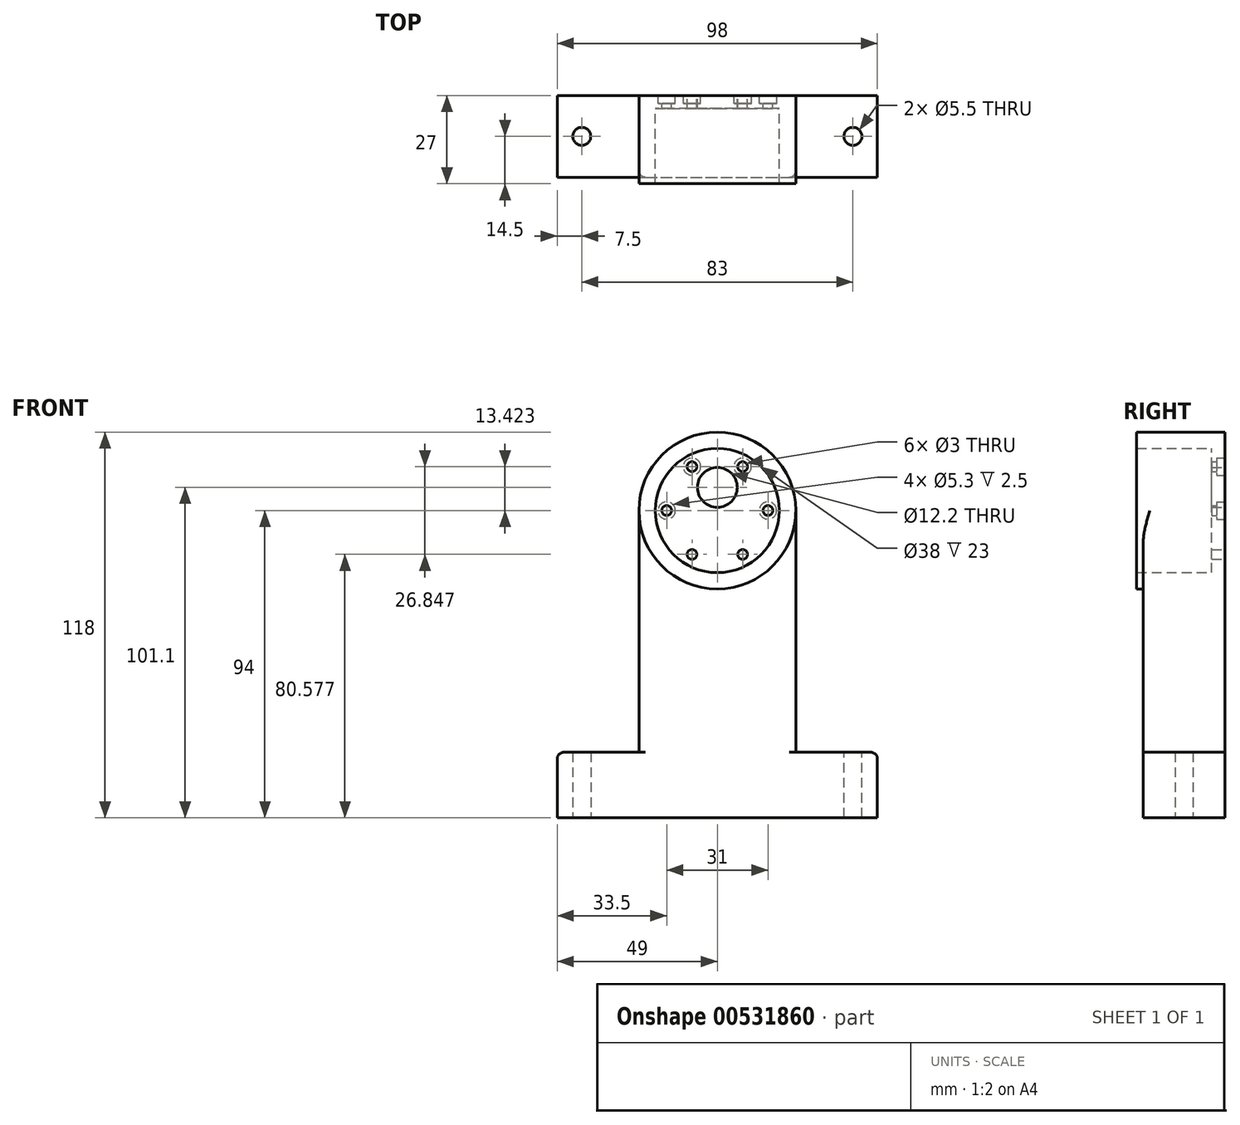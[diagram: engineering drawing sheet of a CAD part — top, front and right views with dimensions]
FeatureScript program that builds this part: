
annotation { "Feature Type Name" : "Feature", "Feature Type Description" : "" }
export const myFeature = defineFeature(function(context is Context, id is Id, definition is map)
    precondition{}
    {
        {
            var Q0;
            Q0=qCreatedBy(makeId("Front.planeOp"),FACE);
            var sketch = newSketch(context, id + "F0", { "sketchPlane" : qUnion([Q0])});
            skCircle(sketch, "E0", {"center": v(0, 0) * mm, "radius": 19 * mm});
            skCircle(sketch, "E1", {"center": v(0, 7.1) * mm, "radius": 6.1 * mm});
            skLineSegment(sketch, "E2", {"start": v(0, 0) * mm, "end": v(15.5, 0) * mm});
            skCircle(sketch, "E3", {"center": v(15.5, 0) * mm, "radius": 1.5 * mm});
            skCircle(sketch, "E4.1.0", {"center": v(7.75, 13.42) * mm, "radius": 1.5 * mm});
            skCircle(sketch, "E4.2.0", {"center": v(-7.75, 13.42) * mm, "radius": 1.5 * mm});
            skCircle(sketch, "E4.3.0", {"center": v(-15.5, 0) * mm, "radius": 1.5 * mm});
            skCircle(sketch, "E4.4.0", {"center": v(-7.75, -13.42) * mm, "radius": 1.5 * mm});
            skCircle(sketch, "E4.5.0", {"center": v(7.75, -13.42) * mm, "radius": 1.5 * mm});
            skSolve(sketch);
        }
        {
            var Q0;
            Q0=qSketchRegion(id+"F0",true);
            extrude(context, id + "F1", {"entities" : qUnion([Q0]), "depth" : 4 * mm});
        }
        {
            var Q0;
            Q0=qCreatedBy(makeId("Front.planeOp"),FACE);
            var sketch = newSketch(context, id + "F2", { "sketchPlane" : qUnion([Q0])});
            skCircle(sketch, "E5", {"center": v(0, 0) * mm, "radius": 19 * mm});
            skCircle(sketch, "E6", {"center": v(0, 0) * mm, "radius": 24 * mm});
            skSolve(sketch);
        }
        {
            var Q0;
            Q0=qSketchRegion(id+"F2",true);
            extrude(context, id + "F3", {"entities" : qUnion([Q0]), "operationType" : NewBodyOperationType.ADD, "depth" : 27 * mm});
        }
        {
            var Q0;
            Q0=makeQuery(id+"F3.boolean.opBoolean","MERGE",FACE,{"derivedFrom":[makeQuery(id+"F1.opExtrude","CAP_FACE",FACE,{"disambiguationData":[OSD([sQuery(id+"F0.wireOp",EDGE,"E0"),sQuery(id+"F0.wireOp",EDGE,"E1"),sQuery(id+"F0.wireOp",EDGE,"E3"),sQuery(id+"F0.wireOp",EDGE,"E4.1.0"),sQuery(id+"F0.wireOp",EDGE,"E4.2.0"),sQuery(id+"F0.wireOp",EDGE,"E4.3.0"),sQuery(id+"F0.wireOp",EDGE,"E4.4.0"),sQuery(id+"F0.wireOp",EDGE,"E4.5.0")])],"isStart":true}),makeQuery(id+"F3.opExtrude","CAP_FACE",FACE,{"disambiguationData":[OSD([sQuery(id+"F2.wireOp",EDGE,"E5"),sQuery(id+"F2.wireOp",EDGE,"E6")])],"isStart":true})]});
            var sketch = newSketch(context, id + "F4", { "sketchPlane" : qUnion([Q0])});
            skLineSegment(sketch, "E7", {"start": v(24, 0) * mm, "end": v(24, -40) * mm});
            skLineSegment(sketch, "E8", {"start": v(24, -40) * mm, "end": v(0, -40) * mm});
            skLineSegment(sketch, "E9", {"start": v(-24, 0) * mm, "end": v(-24, -40) * mm});
            skLineSegment(sketch, "E10", {"start": v(-24, -40) * mm, "end": v(0, -40) * mm});
            skArc(sketch, "E11", {"start": v(-24, 0) * mm, "mid": v(0, -24) * mm, "end": v(24, 0) * mm});
            skSolve(sketch);
        }
        {
            var Q0;
            Q0=qSketchRegion(id+"F4",true);
            extrude(context, id + "F5", {"entities" : qUnion([Q0]), "operationType" : NewBodyOperationType.ADD, "oppositeDirection" : true, "depth" : 25 * mm});
        }
        {
            var Q0;
            Q0=makeQuery(id+"F5.boolean.opBoolean","MERGE",FACE,{"derivedFrom":[makeQuery(id+"F3.boolean.opBoolean","MERGE",FACE,{"derivedFrom":[makeQuery(id+"F1.opExtrude","CAP_FACE",FACE,{"disambiguationData":[OSD([sQuery(id+"F0.wireOp",EDGE,"E0"),sQuery(id+"F0.wireOp",EDGE,"E1"),sQuery(id+"F0.wireOp",EDGE,"E3"),sQuery(id+"F0.wireOp",EDGE,"E4.1.0"),sQuery(id+"F0.wireOp",EDGE,"E4.2.0"),sQuery(id+"F0.wireOp",EDGE,"E4.3.0"),sQuery(id+"F0.wireOp",EDGE,"E4.4.0"),sQuery(id+"F0.wireOp",EDGE,"E4.5.0")])],"isStart":true}),makeQuery(id+"F3.opExtrude","CAP_FACE",FACE,{"disambiguationData":[OSD([sQuery(id+"F2.wireOp",EDGE,"E5"),sQuery(id+"F2.wireOp",EDGE,"E6")])],"isStart":true})]}),makeQuery(id+"F5.opExtrude","CAP_FACE",FACE,{"disambiguationData":[OSD([sQuery(id+"F4.wireOp",EDGE,"E7"),sQuery(id+"F4.wireOp",EDGE,"E8"),sQuery(id+"F4.wireOp",EDGE,"E9"),sQuery(id+"F4.wireOp",EDGE,"E10"),sQuery(id+"F4.wireOp",EDGE,"E11")])],"isStart":true})]});
            var sketch = newSketch(context, id + "F6", { "sketchPlane" : qUnion([Q0])});
            skCircle(sketch, "E12", {"center": v(-7.75, 13.42) * mm, "radius": 2.65 * mm});
            skCircle(sketch, "E13", {"center": v(7.75, 13.42) * mm, "radius": 2.65 * mm});
            skCircle(sketch, "E14", {"center": v(-15.5, 0) * mm, "radius": 2.65 * mm});
            skCircle(sketch, "E15", {"center": v(15.5, 0) * mm, "radius": 2.65 * mm});
            skSolve(sketch);
        }
        {
            var Q0;
            Q0=qSketchRegion(id+"F6",true);
            extrude(context, id + "F7", {"entities" : qUnion([Q0]), "operationType" : NewBodyOperationType.REMOVE, "oppositeDirection" : true, "depth" : 2.5 * mm});
        }
        {
            var Q0;
            Q0=makeQuery(id+"F5.opExtrude","CAP_FACE",FACE,{"disambiguationData":[OSD([sQuery(id+"F4.wireOp",EDGE,"E7"),sQuery(id+"F4.wireOp",EDGE,"E8"),sQuery(id+"F4.wireOp",EDGE,"E9"),sQuery(id+"F4.wireOp",EDGE,"E10"),sQuery(id+"F4.wireOp",EDGE,"E11")])],"isStart":false});
            var sketch = newSketch(context, id + "F8", { "sketchPlane" : qUnion([Q0])});
            skLineSegment(sketch, "E16", {"start": v(0, 0) * mm, "end": v(0, -19) * mm});
            skLineSegment(sketch, "E17", {"start": v(0, -19) * mm, "end": v(0, -94) * mm});
            skPoint(sketch, "E17.endSnap0", {"position": v(0, -40) * mm});
            skLineSegment(sketch, "E18.bottom", {"start": v(0, -94) * mm, "end": v(24, -94) * mm});
            skLineSegment(sketch, "E18.top", {"start": v(0, -40) * mm, "end": v(24, -40) * mm});
            skLineSegment(sketch, "E18.left", {"start": v(0, -94) * mm, "end": v(0, -40) * mm});
            skLineSegment(sketch, "E18.right", {"start": v(24, -94) * mm, "end": v(24, -40) * mm});
            skLineSegment(sketch, "E19.bottom", {"start": v(0, -94) * mm, "end": v(-24, -94) * mm});
            skLineSegment(sketch, "E19.top", {"start": v(0, -40) * mm, "end": v(-24, -40) * mm});
            skLineSegment(sketch, "E19.right", {"start": v(-24, -94) * mm, "end": v(-24, -40) * mm});
            skSolve(sketch);
        }
        {
            var Q0;
            Q0=qSketchRegion(id+"F8",true);
            var Q1;
            Q1=makeQuery(id+"F5.boolean.opBoolean","MERGE",FACE,{"derivedFrom":[makeQuery(id+"F3.boolean.opBoolean","MERGE",FACE,{"derivedFrom":[makeQuery(id+"F1.opExtrude","CAP_FACE",FACE,{"disambiguationData":[OSD([sQuery(id+"F0.wireOp",EDGE,"E0"),sQuery(id+"F0.wireOp",EDGE,"E1"),sQuery(id+"F0.wireOp",EDGE,"E3"),sQuery(id+"F0.wireOp",EDGE,"E4.1.0"),sQuery(id+"F0.wireOp",EDGE,"E4.2.0"),sQuery(id+"F0.wireOp",EDGE,"E4.3.0"),sQuery(id+"F0.wireOp",EDGE,"E4.4.0"),sQuery(id+"F0.wireOp",EDGE,"E4.5.0")])],"isStart":true}),makeQuery(id+"F3.opExtrude","CAP_FACE",FACE,{"disambiguationData":[OSD([sQuery(id+"F2.wireOp",EDGE,"E5"),sQuery(id+"F2.wireOp",EDGE,"E6")])],"isStart":true})]}),makeQuery(id+"F5.opExtrude","CAP_FACE",FACE,{"disambiguationData":[OSD([sQuery(id+"F4.wireOp",EDGE,"E7"),sQuery(id+"F4.wireOp",EDGE,"E8"),sQuery(id+"F4.wireOp",EDGE,"E9"),sQuery(id+"F4.wireOp",EDGE,"E10"),sQuery(id+"F4.wireOp",EDGE,"E11")])],"isStart":true})]});
            extrude(context, id + "F9", {"entities" : qUnion([Q0]), "operationType" : NewBodyOperationType.ADD, "endBound" : BoundingType.UP_TO_SURFACE, "oppositeDirection" : true, "endBoundEntityFace" : qUnion([Q1]), "depth" : 25 * mm});
        }
        {
            var Q0;
            Q0=makeQuery(id+"F9.boolean.opBoolean","MERGE",FACE,{"derivedFrom":[makeQuery(id+"F5.opExtrude","SWEPT_FACE",FACE,{"disambiguationData":[OSD([sQuery(id+"F4.wireOp",EDGE,"E9")])]}),makeQuery(id+"F9.opExtrude","SWEPT_FACE",FACE,{"disambiguationData":[OSD([sQuery(id+"F8.wireOp",EDGE,"E18.right")])]})]});
            var sketch = newSketch(context, id + "F10", { "sketchPlane" : qUnion([Q0])});
            skLineSegment(sketch, "E20.bottom", {"start": v(-25, -94) * mm, "end": v(0, -94) * mm});
            skLineSegment(sketch, "E20.top", {"start": v(-25, -74) * mm, "end": v(0, -74) * mm});
            skLineSegment(sketch, "E20.left", {"start": v(-25, -94) * mm, "end": v(-25, -74) * mm});
            skLineSegment(sketch, "E20.right", {"start": v(0, -94) * mm, "end": v(0, -74) * mm});
            skSolve(sketch);
        }
        {
            var Q0;
            Q0=qSketchRegion(id+"F10",true);
            extrude(context, id + "F11", {"entities" : qUnion([Q0]), "operationType" : NewBodyOperationType.ADD, "depth" : 25 * mm});
        }
        {
            var Q0;
            Q0=makeQuery(id+"F11.opExtrude","SWEPT_FACE",FACE,{"disambiguationData":[OSD([sQuery(id+"F10.wireOp",EDGE,"E20.top")])]});
            var sketch = newSketch(context, id + "F12", { "sketchPlane" : qUnion([Q0])});
            skLineSegment(sketch, "E21", {"start": v(49, -12.5) * mm, "end": v(34, -12.5) * mm});
            skCircle(sketch, "E22", {"center": v(41.5, -12.5) * mm, "radius": 2.75 * mm});
            skSolve(sketch);
        }
        {
            var Q0;
            Q0=makeQuery(id+"F9.boolean.opBoolean","MERGE",FACE,{"derivedFrom":[makeQuery(id+"F5.opExtrude","SWEPT_FACE",FACE,{"disambiguationData":[OSD([sQuery(id+"F4.wireOp",EDGE,"E7")])]}),makeQuery(id+"F9.opExtrude","SWEPT_FACE",FACE,{"disambiguationData":[OSD([sQuery(id+"F8.wireOp",EDGE,"E19.right")])]})]});
            var sketch = newSketch(context, id + "F13", { "sketchPlane" : qUnion([Q0])});
            skLineSegment(sketch, "E23.bottom", {"start": v(25, -94) * mm, "end": v(0, -94) * mm});
            skLineSegment(sketch, "E23.top", {"start": v(25, -74) * mm, "end": v(0, -74) * mm});
            skLineSegment(sketch, "E23.left", {"start": v(25, -94) * mm, "end": v(25, -74) * mm});
            skLineSegment(sketch, "E23.right", {"start": v(0, -94) * mm, "end": v(0, -74) * mm});
            skSolve(sketch);
        }
        {
            var Q0;
            Q0=qSketchRegion(id+"F13",true);
            extrude(context, id + "F14", {"entities" : qUnion([Q0]), "operationType" : NewBodyOperationType.ADD, "depth" : 25 * mm});
        }
        {
            var Q0;
            Q0=makeQuery(id+"F11.opExtrude","CAP_EDGE",EDGE,{"disambiguationData":[OSD([sQuery(id+"F10.wireOp",EDGE,"E20.top")])],"isStart":false});
            var Q1;
            Q1=makeQuery(id+"F14.opExtrude","CAP_EDGE",EDGE,{"disambiguationData":[OSD([sQuery(id+"F13.wireOp",EDGE,"E23.top")])],"isStart":false});
            fillet(context, id + "F15", {"entities" : qUnion([Q0, Q1]), "radius" : 2 * mm, "tangentPropagation" : true, "allowEdgeOverflow" : false});
        }
        {
            var Q0;
            Q0=makeQuery(id+"F14.boolean.opBoolean","MERGE",FACE,{"derivedFrom":[makeQuery(id+"F11.boolean.opBoolean","MERGE",FACE,{"derivedFrom":[makeQuery(id+"F9.opExtrude","SWEPT_FACE",FACE,{"disambiguationData":[OSD([sQuery(id+"F8.wireOp",EDGE,"E18.bottom"),sQuery(id+"F8.wireOp",EDGE,"E19.bottom")])]}),makeQuery(id+"F11.opExtrude","SWEPT_FACE",FACE,{"disambiguationData":[OSD([sQuery(id+"F10.wireOp",EDGE,"E20.bottom")])]})]}),makeQuery(id+"F14.opExtrude","SWEPT_FACE",FACE,{"disambiguationData":[OSD([sQuery(id+"F13.wireOp",EDGE,"E23.bottom")])]})]});
            var sketch = newSketch(context, id + "F16", { "sketchPlane" : qUnion([Q0])});
            skLineSegment(sketch, "E24", {"start": v(-49, 12.5) * mm, "end": v(-34, 12.5) * mm});
            skCircle(sketch, "E25", {"center": v(-41.5, 12.5) * mm, "radius": 2.75 * mm});
            skSolve(sketch);
        }
        {
            var Q0;
            Q0=qSketchRegion(id+"F16",true);
            extrude(context, id + "F17", {"entities" : qUnion([Q0]), "operationType" : NewBodyOperationType.REMOVE, "oppositeDirection" : true, "depth" : 25 * mm});
        }
        {
            var Q0;
            Q0=qSketchRegion(id+"F12",true);
            extrude(context, id + "F18", {"entities" : qUnion([Q0]), "operationType" : NewBodyOperationType.REMOVE, "oppositeDirection" : true, "depth" : 25 * mm});
        }
        {
            var Q0;
            Q0=makeQuery(id+"F9.boolean.opBoolean","MERGE",EDGE,{"derivedFrom":[makeQuery(id+"F5.opExtrude","CAP_EDGE",EDGE,{"disambiguationData":[OSD([sQuery(id+"F4.wireOp",EDGE,"E9")])],"isStart":false}),makeQuery(id+"F9.opExtrude","CAP_EDGE",EDGE,{"disambiguationData":[OSD([sQuery(id+"F8.wireOp",EDGE,"E18.right")])],"isStart":true})]});
            var Q1;
            Q1=makeQuery(id+"F11.opExtrude","CAP_EDGE",EDGE,{"disambiguationData":[OSD([sQuery(id+"F10.wireOp",EDGE,"E20.top")])],"isStart":true});
            var Q2;
            Q2=makeQuery(id+"F14.opExtrude","CAP_EDGE",EDGE,{"disambiguationData":[OSD([sQuery(id+"F13.wireOp",EDGE,"E23.top")])],"isStart":true});
            var Q3;
            Q3=makeQuery(id+"F9.boolean.opBoolean","MERGE",EDGE,{"derivedFrom":[makeQuery(id+"F5.opExtrude","CAP_EDGE",EDGE,{"disambiguationData":[OSD([sQuery(id+"F4.wireOp",EDGE,"E7")])],"isStart":false}),makeQuery(id+"F9.opExtrude","CAP_EDGE",EDGE,{"disambiguationData":[OSD([sQuery(id+"F8.wireOp",EDGE,"E19.right")])],"isStart":true})]});
            fillet(context, id + "F19", {"entities" : qUnion([Q0, Q1, Q2, Q3]), "radius" : 2 * mm, "tangentPropagation" : true, "allowEdgeOverflow" : false});
        }
    });
